FCSTD DOCUMENT  (FreeCAD 0.19R24276 (Git))
Label: Master_sketch_v2
License: All rights reserved
LicenseURL: http://en.wikipedia.org/wiki/All_rights_reserved
objects: Sketcher::SketchObject×6, PartDesign::Body×1
note: 7 computed .brp shape members not serialized (recipe doc carries the construction recipe); baked Part::Feature solids carry a one-line shape summary decoded from their .brp

FEATURE [Sketcher::SketchObject] Sketch  label="Sketch_korzina"
  FullyConstrained = false
  MapMode = 5
  Support = -> [XY_Plane]
  sketch-geometry (21):
    g0: Circle CenterX=0 CenterY=-54 CenterZ=0 NormalX=0 NormalY=0 NormalZ=1 AngleXU=0 Radius=4
    g1: LineSegment StartX=-45 StartY=0 StartZ=0 EndX=-62.2822 EndY=-37.1796 EndZ=0
    g2: LineSegment StartX=45 StartY=0 StartZ=0 EndX=62.2822 EndY=-37.1796 EndZ=0
    g3: LineSegment StartX=-45 StartY=0 StartZ=0 EndX=45 EndY=0 EndZ=0
    g4: LineSegment StartX=0 StartY=0 StartZ=0 EndX=0 EndY=-54 EndZ=0
    g5: Circle CenterX=0 CenterY=0 CenterZ=0 NormalX=0 NormalY=0 NormalZ=1 AngleXU=0 Radius=90
    g6: LineSegment StartX=-45 StartY=0 StartZ=0 EndX=-31.8819 EndY=-39.2255 EndZ=0
    g7: Circle CenterX=0 CenterY=54 CenterZ=0 NormalX=0 NormalY=0 NormalZ=1 AngleXU=0 Radius=4
    g8: LineSegment StartX=0 StartY=0 StartZ=0 EndX=0 EndY=54 EndZ=0
    g9: LineSegment StartX=45 StartY=0 StartZ=0 EndX=56.689 EndY=42.3716 EndZ=0
    g10: LineSegment StartX=-31.8413 StartY=-51.3294 StartZ=0 EndX=-28.0476 EndY=-43.1681 EndZ=0
    g11: LineSegment StartX=-31.8413 StartY=-51.3294 StartZ=0 EndX=-35.6349 EndY=-59.4908 EndZ=0
    g12: Circle CenterX=-45 CenterY=0 CenterZ=0 NormalX=0 NormalY=0 NormalZ=1 AngleXU=0 Radius=41
    g13: Circle CenterX=45 CenterY=0 CenterZ=0 NormalX=0 NormalY=0 NormalZ=1 AngleXU=0 Radius=41
    g14: Circle CenterX=0 CenterY=-54 CenterZ=0 NormalX=0 NormalY=0 NormalZ=1 AngleXU=0 Radius=11
    g15: LineSegment StartX=0 StartY=-54 StartZ=0 EndX=-4.63669 EndY=-63.975 EndZ=0
    g16: LineSegment StartX=-31.8413 StartY=-51.3294 StartZ=0 EndX=-35.6349 EndY=-59.4908 EndZ=0
    g17: LineSegment StartX=62.2822 StartY=-37.1796 StartZ=0 EndX=4.63669 EndY=-63.975 EndZ=0
    g18: LineSegment StartX=4.63669 StartY=-63.975 StartZ=0 EndX=0 EndY=-54 EndZ=0
    g19: LineSegment StartX=-62.2822 StartY=-37.1796 StartZ=0 EndX=-4.63669 EndY=-63.975 EndZ=0
    g20: LineSegment StartX=-31.8413 StartY=-51.3294 StartZ=0 EndX=-62.2822 EndY=-37.1796 EndZ=0
  constraints (45):
    c: Diameter(g0) = 8
    c: Distance(g3) = 90
    c: Coincident(g4,g-1)
    c: Coincident(g4,g0)
    c: Perpendicular(g3,g4)
    c: Distance(g4) = 54
    c: Coincident(g5,g-1)
    c: Diameter(g5) = 180
    c: Coincident(g8,g-1)
    c: Coincident(g8,g7)
    c: Equal(g8,g4)
    c: Parallel(g8,g4)
    c: Coincident(g11,g10)
    c: Symmetric(g11,g10,g10)
    c: Distance(g11,g10) = 18
    c: Coincident(g12,g1)
    c: Coincident(g13,g2)
    c: Equal(g12,g13)
    c: Coincident(g1,g3)
    c: Coincident(g6,g1)
    c: Coincident(g3,g2)
    c: Coincident(g3,g9)
    c: Symmetric(g1,g2,g-1)
    c: Horizontal(g3)
    c: PointOnObject(g1,g12)
    c: Diameter(g12) = 82
    c: Coincident(g14,g0)
    c: Diameter(g14) = 22
    c: PointOnObject(g15,g14)
    c: Coincident(g15,g0)
    c: Coincident(g10,g16)
    c: Distance(g15,g10) = 30
    c: PointOnObject(g2,g13)
    c: Coincident(g17,g2)
    c: PointOnObject(g17,g14)
    c: Coincident(g18,g0)
    c: Perpendicular(g17,g18)
    c: Perpendicular(g17,g2)
    c: Coincident(g19,g1)
    c: Perpendicular(g15,g19)
    c: Perpendicular(g19,g1)
    c: Perpendicular(g10,g19)
    c: Coincident(g20,g10)
    c: Coincident(g20,g1)
    c: Tangent(g20,g12)
FEATURE [PartDesign::Body] Body
  Group = -> [Sketch]
  Origin = -> Origin
FEATURE [Sketcher::SketchObject] Sketch001  label="Sketch001_left"
  FullyConstrained = false
  MapMode = 5
  sketch-geometry (18):
    g0: LineSegment StartX=-45 StartY=0 StartZ=0 EndX=45 EndY=0 EndZ=0
    g1: LineSegment StartX=0 StartY=0 StartZ=0 EndX=0 EndY=-54 EndZ=0
    g2: Circle CenterX=0 CenterY=54 CenterZ=0 NormalX=0 NormalY=0 NormalZ=1 AngleXU=0 Radius=4
    g3: LineSegment StartX=0 StartY=0 StartZ=0 EndX=0 EndY=54 EndZ=0
    g4: Circle CenterX=0 CenterY=220 CenterZ=0 NormalX=0 NormalY=0 NormalZ=1 AngleXU=0 Radius=20
    g5: LineSegment StartX=1.97542 StartY=-120.078 StartZ=0 EndX=-81.7197 EndY=-81.8796 EndZ=0
    g6: LineSegment StartX=-81.7197 StartY=-81.8796 StartZ=0 EndX=-106.606 EndY=-84.2618 EndZ=0
    g7: LineSegment StartX=-106.606 StartY=-84.2618 StartZ=0 EndX=-106.892 EndY=-81.2754 EndZ=0
    g8: LineSegment StartX=-106.892 StartY=-81.2754 StartZ=0 EndX=-82.0055 EndY=-78.8932 EndZ=0
    g9: LineSegment StartX=-82.0055 StartY=-78.8932 StartZ=0 EndX=-81.7197 EndY=-81.8796 EndZ=0
    g10: LineSegment StartX=-18.9589 StartY=-118.419 StartZ=0 EndX=22.9098 EndY=-121.738 EndZ=0
    g11: LineSegment StartX=22.9098 StartY=-121.738 StartZ=0 EndX=22.5147 EndY=-126.722 EndZ=0
    g12: LineSegment StartX=-19.354 StartY=-123.403 StartZ=0 EndX=-18.9589 EndY=-118.419 EndZ=0
    g13: LineSegment StartX=-18.9589 StartY=-118.419 StartZ=0 EndX=-81.7197 EndY=-81.8796 EndZ=0
    g14: LineSegment StartX=-19.354 StartY=-123.403 StartZ=0 EndX=-106.606 EndY=-84.2618 EndZ=0
    g15: LineSegment StartX=-19.354 StartY=-123.403 StartZ=0 EndX=22.5147 EndY=-126.722 EndZ=0
    g16: Circle CenterX=0 CenterY=-145 CenterZ=0 NormalX=0 NormalY=0 NormalZ=1 AngleXU=0 Radius=4
    g17: LineSegment StartX=0 StartY=-145 StartZ=0 EndX=1.97542 EndY=-120.078 EndZ=0
  constraints (47):
    c: Distance(g0) = 90
    c: Coincident(g1,g-1)
    c: Perpendicular(g0,g1)
    c: Distance(g1) = 54
    c: Coincident(g3,g-1)
    c: Coincident(g3,g2)
    c: Equal(g3,g1)
    c: Parallel(g3,g1)
    c: PointOnObject(g4,g-2)
    c: Radius(g4) = 20
    c: DistanceY(g-1,g4) = 220
    c: Distance(g5) = 92
    c: Coincident(g6,g5)
    c: Coincident(g8,g7)
    c: Coincident(g9,g8)
    c: Coincident(g9,g5)
    c: Parallel(g7,g9)
    c: Perpendicular(g7,g6)
    c: Distance(g6) = 25
    c: Symmetric(g0,g0,g-1)
    c: Horizontal(g0)
    c: Parallel(g6,g8)
    c: Angle(g6,g5) = 2.61799
    c: Coincident(g10,g11)
    c: Coincident(g12,g10)
    c: Symmetric(g10,g10,g5)
    c: Coincident(g13,g10)
    c: Coincident(g13,g5)
    c: Coincident(g14,g6)
    c: Coincident(g7,g6)
    c: Distance(g7) = 3
    c: Perpendicular(g11,g10)
    c: Angle(g5,g10) = 0.349066
    c: Equal(g12,g11)
    c: Coincident(g15,g14)
    c: Coincident(g15,g11)
    c: Coincident(g14,g12)
    c: Perpendicular(g15,g12)
    c: Distance(g14,g11) = 42
    c: Distance(g10,g11) = 5
    c: PointOnObject(g16,g-2)
    c: Diameter(g16) = 8
    c: Coincident(g17,g16)
    c: Coincident(g17,g5)
    c: Perpendicular(g15,g17)
    c: Distance(g16,g17) = 25
    c: DistanceY(g16,g-1) = 145
FEATURE [Sketcher::SketchObject] Sketch020  label="Sketch020_right"
  FullyConstrained = false
  MapMode = 5
  sketch-geometry (46):
    g0: Circle CenterX=0 CenterY=-54 CenterZ=0 NormalX=0 NormalY=0 NormalZ=1 AngleXU=0 Radius=4
    g1: LineSegment StartX=-57.9645 StartY=-38.8963 StartZ=0 EndX=-1.26483 EndY=-57.7948 EndZ=0
    g2: LineSegment StartX=-45 StartY=0 StartZ=0 EndX=-57.9645 EndY=-38.8963 EndZ=0
    g3: LineSegment StartX=0 StartY=-54 StartZ=0 EndX=-1.26483 EndY=-57.7948 EndZ=0
    g4: LineSegment StartX=1.39757 StartY=-57.7479 StartZ=0 EndX=58.5823 EndY=-36.4241 EndZ=0
    g5: LineSegment StartX=45 StartY=0 StartZ=0 EndX=58.5823 EndY=-36.4241 EndZ=0
    g6: LineSegment StartX=0 StartY=-54 StartZ=0 EndX=1.39757 EndY=-57.7479 EndZ=0
    g7: LineSegment StartX=-45 StartY=0 StartZ=0 EndX=45 EndY=0 EndZ=0
    g8: LineSegment StartX=0 StartY=0 StartZ=0 EndX=0 EndY=-54 EndZ=0
    g9: Circle CenterX=0 CenterY=0 CenterZ=0 NormalX=0 NormalY=0 NormalZ=1 AngleXU=0 Radius=90
    g10: LineSegment StartX=-45 StartY=0 StartZ=0 EndX=-31.8819 EndY=-39.2255 EndZ=0
    g11: Circle CenterX=0 CenterY=54 CenterZ=0 NormalX=0 NormalY=0 NormalZ=1 AngleXU=0 Radius=4
    g12: LineSegment StartX=0 StartY=0 StartZ=0 EndX=0 EndY=54 EndZ=0
    g13: Circle CenterX=0 CenterY=220 CenterZ=0 NormalX=0 NormalY=0 NormalZ=1 AngleXU=0 Radius=20
    g14: LineSegment StartX=45 StartY=0 StartZ=0 EndX=56.689 EndY=42.3716 EndZ=0
    g15: LineSegment StartX=-29.7255 StartY=-48.3086 StartZ=0 EndX=-26.8797 EndY=-39.7704 EndZ=0
    g16: LineSegment StartX=-29.7255 StartY=-48.3086 StartZ=0 EndX=-32.5714 EndY=-56.8468 EndZ=0
    g17: Circle CenterX=-45 CenterY=0 CenterZ=0 NormalX=0 NormalY=0 NormalZ=1 AngleXU=0 Radius=41
    g18: Circle CenterX=45 CenterY=0 CenterZ=0 NormalX=0 NormalY=0 NormalZ=1 AngleXU=0 Radius=41
    g19: LineSegment StartX=0 StartY=0 StartZ=0 EndX=0 EndY=-135 EndZ=0
    g20: LineSegment StartX=0 StartY=-135 StartZ=0 EndX=-86.4517 EndY=-103.534 EndZ=0
    g21: LineSegment StartX=0 StartY=-135 StartZ=0 EndX=86.4517 EndY=-103.534 EndZ=0
    g22: LineSegment StartX=-86.4517 StartY=-103.534 StartZ=0 EndX=-111.072 EndY=-107.875 EndZ=0
    g23: LineSegment StartX=-111.072 StartY=-107.875 StartZ=0 EndX=-111.593 EndY=-104.921 EndZ=0
    g24: LineSegment StartX=-111.593 StartY=-104.921 StartZ=0 EndX=-86.9727 EndY=-100.58 EndZ=0
    g25: LineSegment StartX=-86.9727 StartY=-100.58 StartZ=0 EndX=-86.4517 EndY=-103.534 EndZ=0
    g26: LineSegment StartX=-21 StartY=-135 StartZ=0 EndX=21 EndY=-135 EndZ=0
    g27: LineSegment StartX=21 StartY=-135 StartZ=0 EndX=21 EndY=-140 EndZ=0
    g28: LineSegment StartX=21 StartY=-140 StartZ=0 EndX=-21 EndY=-140 EndZ=0
    g29: LineSegment StartX=-21 StartY=-140 StartZ=0 EndX=-21 EndY=-135 EndZ=0
    g30: LineSegment StartX=0 StartY=-135 StartZ=0 EndX=-72.9805 EndY=-135 EndZ=0
    g31: LineSegment StartX=-21 StartY=-135 StartZ=0 EndX=-86.4517 EndY=-103.534 EndZ=0
    g32: LineSegment StartX=-21 StartY=-140 StartZ=0 EndX=-111.072 EndY=-107.875 EndZ=0
    g33: LineSegment StartX=-110.377 StartY=-111.815 StartZ=0 EndX=-61.9528 EndY=-103.276 EndZ=0
    g34: LineSegment StartX=-111.072 StartY=-107.875 StartZ=0 EndX=-110.377 EndY=-111.815 EndZ=0
    g35: LineSegment StartX=-86.9727 StartY=-100.58 StartZ=0 EndX=118.679 EndY=-100.58 EndZ=0
    g36: LineSegment StartX=86.4517 StartY=-103.534 StartZ=0 EndX=111.072 EndY=-107.875 EndZ=0
    g37: LineSegment StartX=111.072 StartY=-107.875 StartZ=0 EndX=111.593 EndY=-104.921 EndZ=0
    g38: LineSegment StartX=111.593 StartY=-104.921 StartZ=0 EndX=86.9727 EndY=-100.58 EndZ=0
    g39: LineSegment StartX=86.9727 StartY=-100.58 StartZ=0 EndX=86.4517 EndY=-103.534 EndZ=0
    g40: LineSegment StartX=21 StartY=-135 StartZ=0 EndX=-21 EndY=-135 EndZ=0
    g41: LineSegment StartX=-21 StartY=-135 StartZ=0 EndX=-21 EndY=-130 EndZ=0
    g42: LineSegment StartX=-21 StartY=-130 StartZ=0 EndX=21 EndY=-130 EndZ=0
    g43: LineSegment StartX=21 StartY=-130 StartZ=0 EndX=21 EndY=-135 EndZ=0
    g44: LineSegment StartX=21 StartY=-135 StartZ=0 EndX=111.072 EndY=-107.875 EndZ=0
    g45: LineSegment StartX=21 StartY=-130 StartZ=0 EndX=86.4517 EndY=-103.534 EndZ=0
  constraints (115):
    c: Diameter(g0) = 8
    c: PointOnObject(g1,g0)
    c: Perpendicular(g1,g2)
    c: Coincident(g3,g0)
    c: Coincident(g3,g1)
    c: Perpendicular(g3,g1)
    c: PointOnObject(g4,g0)
    c: Coincident(g5,g4)
    c: Perpendicular(g5,g4)
    c: Coincident(g6,g0)
    c: Coincident(g6,g4)
    c: Perpendicular(g4,g6)
    c: Distance(g7) = 90
    c: Coincident(g8,g-1)
    c: Coincident(g8,g0)
    c: Perpendicular(g7,g8)
    c: Distance(g8) = 54
    c: Coincident(g9,g-1)
    c: Diameter(g9) = 180
    c: Equal(g0,g11)
    c: Coincident(g12,g-1)
    c: Coincident(g12,g11)
    c: Equal(g12,g8)
    c: Parallel(g12,g8)
    c: PointOnObject(g13,g-2)
    c: Radius(g13) = 20
    c: DistanceY(g-1,g13) = 220
    c: PointOnObject(g15,g1)
    c: Coincident(g16,g15)
    c: Symmetric(g16,g15,g15)
    c: Distance(g16,g15) = 18
    c: Perpendicular(g15,g1)
    c: Distance(g15,g1) = 30
    c: Coincident(g17,g2)
    c: Coincident(g18,g5)
    c: Equal(g17,g18)
    c: Coincident(g19,g-1)
    c: Vertical(g19)
    c: DistanceY(g19,g19) = 135
    c: Coincident(g20,g21)
    c: Coincident(g20,g19)
    c: Distance(g20) = 92
    c: Equal(g20,g21)
    c: Coincident(g22,g20)
    c: Coincident(g24,g23)
    c: Coincident(g25,g24)
    c: Coincident(g25,g20)
    c: Parallel(g23,g25)
    c: Perpendicular(g23,g22)
    c: Distance(g22) = 25
    c: Coincident(g2,g7)
    c: Coincident(g10,g2)
    c: Coincident(g7,g5)
    c: Coincident(g7,g14)
    c: Symmetric(g2,g5,g-1)
    c: Horizontal(g7)
    c: PointOnObject(g2,g17)
    c: Coincident(g1,g2)
    c: Diameter(g17) = 82
    c: Parallel(g22,g24)
    c: Angle(g22,g20) = 2.61799
    c: Coincident(g26,g27)
    c: Coincident(g27,g28)
    c: Coincident(g28,g29)
    c: Coincident(g29,g26)
    c: Horizontal(g26)
    c: Horizontal(g28)
    c: Vertical(g27)
    c: Vertical(g29)
    c: Coincident(g30,g20)
    c: Horizontal(g30)
    c: Angle(g20,g30) = 0.349066
    c: DistanceX(g28,g28) = 42
    c: Symmetric(g26,g26,g20)
    c: DistanceY(g27,g27) = 5
    c: Coincident(g31,g26)
    c: Coincident(g31,g20)
    c: Coincident(g32,g28)
    c: Coincident(g32,g22)
    c: Coincident(g23,g22)
    c: Distance(g23) = 3
    c: Parallel(g22,g33)
    c: Coincident(g34,g23)
    c: Perpendicular(g34,g33)
    c: Coincident(g33,g34)
    c: Distance(g34) = 4
    c: Coincident(g35,g24)
    c: Horizontal(g35)
    c: Coincident(g38,g37)
    c: Coincident(g39,g38)
    c: Parallel(g37,g39)
    c: Perpendicular(g37,g36)
    c: Distance(g36) = 25
    c: Parallel(g36,g38)
    c: Coincident(g37,g36)
    c: Distance(g37) = 3
    c: Coincident(g21,g39)
    c: Angle(g21,g30) = 2.79253
    c: Coincident(g40,g41)
    c: Coincident(g41,g42)
    c: Coincident(g42,g43)
    c: Coincident(g43,g40)
    c: Horizontal(g40)
    c: Horizontal(g42)
    c: Vertical(g41)
    c: Vertical(g43)
    c: Coincident(g40,g26)
    c: DistanceY(g43,g43) = 5
    c: Vertical(g41,g26)
    c: Coincident(g44,g26)
    c: Coincident(g44,g37)
    c: Coincident(g45,g42)
    c: Coincident(g45,g39)
    c: Coincident(g36,g39)
    c: Angle(g21,g36) = 2.61799
FEATURE [Sketcher::SketchObject] Sketch021  label="Sketch001_left_right_lips"
  FullyConstrained = false
  MapMode = 5
  sketch-geometry (31):
    g0: LineSegment StartX=-1.5074 StartY=-120.045 StartZ=0 EndX=-89.6991 EndY=-93.8496 EndZ=0
    g1: LineSegment StartX=-89.6991 StartY=-93.8496 StartZ=0 EndX=-114.013 EndY=-99.6674 EndZ=0
    g2: LineSegment StartX=-114.013 StartY=-99.6674 StartZ=0 EndX=-114.711 EndY=-96.7497 EndZ=0
    g3: LineSegment StartX=-114.711 StartY=-96.7497 StartZ=0 EndX=-90.3972 EndY=-90.9319 EndZ=0
    g4: LineSegment StartX=-90.3972 StartY=-90.9319 StartZ=0 EndX=-89.6991 EndY=-93.8496 EndZ=0
    g5: LineSegment StartX=-22.4692 StartY=-121.312 StartZ=0 EndX=19.4544 EndY=-118.779 EndZ=0
    g6: LineSegment StartX=19.4544 StartY=-118.779 StartZ=0 EndX=19.7559 EndY=-123.77 EndZ=0
    g7: LineSegment StartX=-22.1677 StartY=-126.303 StartZ=0 EndX=-22.4692 EndY=-121.312 EndZ=0
    g8: LineSegment StartX=-22.4692 StartY=-121.312 StartZ=0 EndX=-89.6991 EndY=-93.8496 EndZ=0
    g9: LineSegment StartX=-22.1677 StartY=-126.303 StartZ=0 EndX=-114.013 EndY=-99.6674 EndZ=0
    g10: LineSegment StartX=-22.1677 StartY=-126.303 StartZ=0 EndX=19.7559 EndY=-123.77 EndZ=0
    g11: Circle CenterX=0 CenterY=-145 CenterZ=0 NormalX=0 NormalY=0 NormalZ=1 AngleXU=0 Radius=4
    g12: LineSegment StartX=0 StartY=-145 StartZ=0 EndX=-1.5074 EndY=-120.045 EndZ=0
    g13: LineSegment StartX=-22.4692 StartY=-121.312 StartZ=0 EndX=-22.7707 EndY=-116.321 EndZ=0
    g14: LineSegment StartX=19.1529 StartY=-113.788 StartZ=0 EndX=19.4544 EndY=-118.779 EndZ=0
    g15: LineSegment StartX=-22.7707 StartY=-116.321 StartZ=0 EndX=19.1529 EndY=-113.788 EndZ=0
    g16: LineSegment StartX=-1.5074 StartY=-120.045 StartZ=0 EndX=82.8898 EndY=-83.4242 EndZ=0
    g17: LineSegment StartX=82.8898 StartY=-83.4242 StartZ=0 EndX=107.727 EndY=-86.273 EndZ=0
    g18: LineSegment StartX=82.8898 StartY=-83.4242 StartZ=0 EndX=83.2316 EndY=-80.4437 EndZ=0
    g19: LineSegment StartX=107.727 StartY=-86.273 StartZ=0 EndX=108.069 EndY=-83.2925 EndZ=0
    g20: LineSegment StartX=108.069 StartY=-83.2925 StartZ=0 EndX=83.2316 EndY=-80.4437 EndZ=0
    g21: LineSegment StartX=19.4544 StartY=-118.779 StartZ=0 EndX=107.727 EndY=-86.273 EndZ=0
    g22: LineSegment StartX=19.1529 StartY=-113.788 StartZ=0 EndX=82.8898 EndY=-83.4242 EndZ=0
    g23: LineSegment StartX=-114.711 StartY=-96.7497 StartZ=0 EndX=-120.296 EndY=-73.4087 EndZ=0
    g24: LineSegment StartX=-120.296 StartY=-73.4087 StartZ=0 EndX=-95.9823 EndY=-67.5908 EndZ=0
    g25: LineSegment StartX=-95.9823 StartY=-67.5908 StartZ=0 EndX=-90.3972 EndY=-90.9319 EndZ=0
    g26: LineSegment StartX=-117.038 StartY=-87.0243 StartZ=0 EndX=-92.7244 EndY=-81.2065 EndZ=0
    g27: LineSegment StartX=83.2316 StartY=-80.4437 StartZ=0 EndX=85.9665 EndY=-56.6001 EndZ=0
    g28: LineSegment StartX=85.9665 StartY=-56.6001 StartZ=0 EndX=110.804 EndY=-59.4489 EndZ=0
    g29: LineSegment StartX=110.804 StartY=-59.4489 StartZ=0 EndX=108.069 EndY=-83.2925 EndZ=0
    g30: LineSegment StartX=84.3711 StartY=-70.5089 StartZ=0 EndX=109.208 EndY=-73.3577 EndZ=0
  constraints (84):
    c: Distance(g0) = 92
    c: Coincident(g1,g0)
    c: Coincident(g3,g2)
    c: Coincident(g4,g3)
    c: Coincident(g4,g0)
    c: Parallel(g2,g4)
    c: Perpendicular(g2,g1)
    c: Distance(g1) = 25
    c: Parallel(g1,g3)
    c: Angle(g1,g0) = 2.61799
    c: Coincident(g5,g6)
    c: Coincident(g7,g5)
    c: Symmetric(g5,g5,g0)
    c: Coincident(g8,g5)
    c: Coincident(g8,g0)
    c: Coincident(g9,g1)
    c: Coincident(g2,g1)
    c: Distance(g2) = 3
    c: Perpendicular(g6,g5)
    c: Angle(g0,g5) = 0.349066
    c: Equal(g7,g6)
    c: Coincident(g10,g9)
    c: Coincident(g10,g6)
    c: Coincident(g9,g7)
    c: Perpendicular(g10,g7)
    c: Distance(g9,g6) = 42
    c: Distance(g5,g6) = 5
    c: PointOnObject(g11,g-2)
    c: Diameter(g11) = 8
    c: Coincident(g12,g11)
    c: Coincident(g12,g0)
    c: Perpendicular(g10,g12)
    c: Distance(g11,g12) = 25
    c: DistanceY(g11,g-1) = 145
    c: Coincident(g13,g5)
    c: Perpendicular(g13,g5)
    c: Distance(g13) = 5
    c: Coincident(g14,g5)
    c: Coincident(g15,g13)
    c: Parallel(g15,g5)
    c: Equal(g15,g5)
    c: Coincident(g14,g15)
    c: Coincident(g16,g12)
    c: Angle(g5,g16) = 0.349066
    c: Equal(g16,g0)
    c: Coincident(g17,g16)
    c: Angle(g16,g17) = 2.61799
    c: Coincident(g18,g16)
    c: Coincident(g19,g17)
    c: Perpendicular(g17,g18)
    c: Perpendicular(g17,g19)
    c: Distance(g19) = 3
    c: Coincident(g20,g19)
    c: Coincident(g20,g18)
    c: Equal(g18,g19)
    c: Distance(g16,g17) = 25
    c: Coincident(g21,g5)
    c: Coincident(g21,g17)
    c: Coincident(g22,g14)
    c: Coincident(g22,g16)
    c: Coincident(g23,g2)
    c: Coincident(g24,g23)
    c: Coincident(g25,g3)
    c: Perpendicular(g23,g3)
    c: Coincident(g24,g25)
    c: Perpendicular(g25,g3)
    c: Equal(g23,g25)
    c: Distance(g23) = 24
    c: Parallel(g24,g26)
    c: PointOnObject(g26,g23)
    c: PointOnObject(g26,g25)
    c: Distance(g2,g26) = 10
    c: Coincident(g27,g18)
    c: Coincident(g28,g27)
    c: Coincident(g29,g28)
    c: Coincident(g29,g19)
    c: Perpendicular(g27,g20)
    c: Perpendicular(g20,g29)
    c: Parallel(g28,g20)
    c: Distance(g27) = 24
    c: PointOnObject(g30,g27)
    c: PointOnObject(g30,g29)
    c: Distance(g30,g18) = 10
    c: Parallel(g30,g28)
FEATURE [Sketcher::SketchObject] Sketch022  label="Sketch001_left_right_lips001"
  FullyConstrained = false
  MapMode = 5
  sketch-geometry (48):
    g0: LineSegment StartX=3.7328 StartY=-120.28 StartZ=0 EndX=-77.0516 EndY=-76.2588 EndZ=0
    g1: LineSegment StartX=-77.0516 StartY=-76.2588 StartZ=0 EndX=-102.044 EndY=-76.8753 EndZ=0
    g2: LineSegment StartX=-102.044 StartY=-76.8753 StartZ=0 EndX=-102.118 EndY=-73.8762 EndZ=0
    g3: LineSegment StartX=-102.118 StartY=-73.8762 StartZ=0 EndX=-77.1256 EndY=-73.2598 EndZ=0
    g4: LineSegment StartX=-77.1256 StartY=-73.2598 StartZ=0 EndX=-77.0516 EndY=-76.2588 EndZ=0
    g5: LineSegment StartX=-17.0318 StartY=-117.145 StartZ=0 EndX=24.4974 EndY=-123.416 EndZ=0
    g6: LineSegment StartX=24.4974 StartY=-123.416 StartZ=0 EndX=23.7508 EndY=-128.36 EndZ=0
    g7: LineSegment StartX=-17.7784 StartY=-122.089 StartZ=0 EndX=-17.0318 EndY=-117.145 EndZ=0
    g8: LineSegment StartX=-17.0318 StartY=-117.145 StartZ=0 EndX=-77.0516 EndY=-76.2588 EndZ=0
    g9: LineSegment StartX=-17.7784 StartY=-122.089 StartZ=0 EndX=-102.044 EndY=-76.8753 EndZ=0
    g10: LineSegment StartX=-17.7784 StartY=-122.089 StartZ=0 EndX=23.7508 EndY=-128.36 EndZ=0
    g11: Circle CenterX=0 CenterY=-145 CenterZ=0 NormalX=0 NormalY=0 NormalZ=1 AngleXU=0 Radius=4
    g12: LineSegment StartX=0 StartY=-145 StartZ=0 EndX=3.7328 EndY=-120.28 EndZ=0
    g13: LineSegment StartX=-17.0318 StartY=-117.145 StartZ=0 EndX=-16.2852 EndY=-112.201 EndZ=0
    g14: LineSegment StartX=25.244 StartY=-118.472 StartZ=0 EndX=24.4974 EndY=-123.416 EndZ=0
    g15: LineSegment StartX=-16.2852 StartY=-112.201 StartZ=0 EndX=25.244 EndY=-118.472 EndZ=0
    g16: LineSegment StartX=3.7328 StartY=-120.28 StartZ=0 EndX=93.9136 EndY=-102.075 EndZ=0
    g17: LineSegment StartX=93.9136 StartY=-102.075 StartZ=0 EndX=117.61 EndY=-110.044 EndZ=0
    g18: LineSegment StartX=93.9136 StartY=-102.075 StartZ=0 EndX=94.8699 EndY=-99.2319 EndZ=0
    g19: LineSegment StartX=117.61 StartY=-110.044 StartZ=0 EndX=118.566 EndY=-107.201 EndZ=0
    g20: LineSegment StartX=118.566 StartY=-107.201 StartZ=0 EndX=94.8699 EndY=-99.2319 EndZ=0
    g21: LineSegment StartX=24.4974 StartY=-123.416 StartZ=0 EndX=117.61 EndY=-110.044 EndZ=0
    g22: LineSegment StartX=25.244 StartY=-118.472 StartZ=0 EndX=93.9136 EndY=-102.075 EndZ=0
    g23: LineSegment StartX=-102.118 StartY=-73.8762 StartZ=0 EndX=-102.71 EndY=-49.8835 EndZ=0
    g24: LineSegment StartX=-102.71 StartY=-49.8835 StartZ=0 EndX=-77.7173 EndY=-49.2671 EndZ=0
    g25: LineSegment StartX=-77.7173 StartY=-49.2671 StartZ=0 EndX=-77.1256 EndY=-73.2598 EndZ=0
    g26: LineSegment StartX=-102.365 StartY=-63.8792 StartZ=0 EndX=-77.3721 EndY=-63.2628 EndZ=0
    g27: LineSegment StartX=94.8699 StartY=-99.2319 StartZ=0 EndX=102.52 EndY=-76.4837 EndZ=0
    g28: LineSegment StartX=102.52 StartY=-76.4837 StartZ=0 EndX=126.216 EndY=-84.4523 EndZ=0
    g29: LineSegment StartX=126.216 StartY=-84.4523 StartZ=0 EndX=118.566 EndY=-107.201 EndZ=0
    g30: LineSegment StartX=98.0573 StartY=-89.7535 StartZ=0 EndX=121.753 EndY=-97.7221 EndZ=0
    g31: Circle CenterX=-78.9071 CenterY=-93.0839 CenterZ=0 NormalX=0 NormalY=0 NormalZ=1 AngleXU=0 Radius=11
    g32: LineSegment StartX=3.7328 StartY=-120.28 StartZ=0 EndX=-78.9071 EndY=-93.0839 EndZ=0
    g33: LineSegment StartX=-78.9071 StartY=-93.0839 StartZ=0 EndX=64.3834 EndY=-48.7235 EndZ=0
    g34: LineSegment StartX=-79.7943 StartY=-90.2181 StartZ=0 EndX=63.4962 EndY=-45.8577 EndZ=0
    g35: LineSegment StartX=64.3834 StartY=-48.7235 StartZ=0 EndX=63.4962 EndY=-45.8577 EndZ=0
    g36: LineSegment StartX=-78.9071 StartY=-93.0839 StartZ=0 EndX=-79.7943 EndY=-90.2181 EndZ=0
    g37: Circle CenterX=0 CenterY=-54 CenterZ=0 NormalX=0 NormalY=0 NormalZ=1 AngleXU=0 Radius=11
    g38: LineSegment StartX=0 StartY=-54 StartZ=0 EndX=3.25309 EndY=-64.508 EndZ=0
    g39: LineSegment StartX=3.25309 StartY=-64.508 StartZ=0 EndX=63.4962 EndY=-45.8577 EndZ=0
    g40: Circle CenterX=-78.9071 CenterY=-93.0839 CenterZ=0 NormalX=0 NormalY=0 NormalZ=1 AngleXU=0 Radius=14
    g41: Circle CenterX=-78.9071 CenterY=-93.0839 CenterZ=0 NormalX=0 NormalY=0 NormalZ=1 AngleXU=0 Radius=2.5
    g42: LineSegment StartX=-41.5835 StartY=-78.3886 StartZ=0 EndX=-39.8091 EndY=-84.1203 EndZ=0
    g43: LineSegment StartX=-39.8091 StartY=-84.1203 StartZ=0 EndX=65.2706 EndY=-51.5893 EndZ=0
    g44: LineSegment StartX=64.3834 StartY=-48.7235 StartZ=0 EndX=65.2706 EndY=-51.5893 EndZ=0
    g45: LineSegment StartX=-78.9071 StartY=-93.0839 StartZ=0 EndX=-92.4492 EndY=-114.098 EndZ=0
    g46: LineSegment StartX=-17.7784 StartY=-122.089 StartZ=0 EndX=-55.7737 EndY=-109.585 EndZ=0
    g47: LineSegment StartX=-55.7737 StartY=-109.585 StartZ=0 EndX=-60.4628 EndY=-123.833 EndZ=0
  constraints (130):
    c: Distance(g0) = 92
    c: Coincident(g1,g0)
    c: Coincident(g3,g2)
    c: Coincident(g4,g3)
    c: Coincident(g4,g0)
    c: Parallel(g2,g4)
    c: Perpendicular(g2,g1)
    c: Distance(g1) = 25
    c: Parallel(g1,g3)
    c: Angle(g1,g0) = 2.61799
    c: Coincident(g5,g6)
    c: Coincident(g7,g5)
    c: Symmetric(g5,g5,g0)
    c: Coincident(g8,g5)
    c: Coincident(g8,g0)
    c: Coincident(g9,g1)
    c: Coincident(g2,g1)
    c: Distance(g2) = 3
    c: Perpendicular(g6,g5)
    c: Angle(g0,g5) = 0.349066
    c: Equal(g7,g6)
    c: Coincident(g10,g9)
    c: Coincident(g10,g6)
    c: Coincident(g9,g7)
    c: Perpendicular(g10,g7)
    c: Distance(g9,g6) = 42
    c: Distance(g5,g6) = 5
    c: PointOnObject(g11,g-2)
    c: Diameter(g11) = 8
    c: Coincident(g12,g11)
    c: Coincident(g12,g0)
    c: Perpendicular(g10,g12)
    c: Distance(g11,g12) = 25
    c: DistanceY(g11,g-1) = 145
    c: Coincident(g13,g5)
    c: Perpendicular(g13,g5)
    c: Distance(g13) = 5
    c: Coincident(g14,g5)
    c: Coincident(g15,g13)
    c: Parallel(g15,g5)
    c: Equal(g15,g5)
    c: Coincident(g14,g15)
    c: Coincident(g16,g12)
    c: Angle(g5,g16) = 0.349066
    c: Equal(g16,g0)
    c: Coincident(g17,g16)
    c: Angle(g16,g17) = 2.61799
    c: Coincident(g18,g16)
    c: Coincident(g19,g17)
    c: Perpendicular(g17,g18)
    c: Perpendicular(g17,g19)
    c: Distance(g19) = 3
    c: Coincident(g20,g19)
    c: Coincident(g20,g18)
    c: Equal(g18,g19)
    c: Distance(g16,g17) = 25
    c: Coincident(g21,g5)
    c: Coincident(g21,g17)
    c: Coincident(g22,g14)
    c: Coincident(g22,g16)
    c: Coincident(g23,g2)
    c: Coincident(g24,g23)
    c: Coincident(g25,g3)
    c: Perpendicular(g23,g3)
    c: Coincident(g24,g25)
    c: Perpendicular(g25,g3)
    c: Equal(g23,g25)
    c: Distance(g23) = 24
    c: Parallel(g24,g26)
    c: PointOnObject(g26,g23)
    c: PointOnObject(g26,g25)
    c: Distance(g2,g26) = 10
    c: Coincident(g27,g18)
    c: Coincident(g28,g27)
    c: Coincident(g29,g28)
    c: Coincident(g29,g19)
    c: Perpendicular(g27,g20)
    c: Perpendicular(g20,g29)
    c: Parallel(g28,g20)
    c: Distance(g27) = 24
    c: PointOnObject(g30,g27)
    c: PointOnObject(g30,g29)
    c: Distance(g30,g18) = 10
    c: Parallel(g30,g28)
    c: Coincident(g32,g12)
    c: Coincident(g32,g31)
    c: Coincident(g33,g31)
    c: Distance(g32) = 87
    c: Distance(g33) = 150
    c: Angle(g9,g32) = 0.174533
    c: Coincident(g35,g33)
    c: Coincident(g35,g34)
    c: Perpendicular(g33,g35)
    c: Distance(g35) = 3
    c: Parallel(g34,g33)
    c: Coincident(g36,g31)
    c: Perpendicular(g33,g36)
    c: Coincident(g36,g34)
    c: PointOnObject(g37,g-2)
    c: DistanceY(g11,g37) = 91
    c: Coincident(g38,g37)
    c: PointOnObject(g38,g37)
    c: Coincident(g39,g38)
    c: Coincident(g39,g34)
    c: Parallel(g39,g34)
    c: Diameter(g37) = 22
    c: Perpendicular(g38,g34)
    c: Equal(g31,g37)
    c: Coincident(g40,g31)
    c: Diameter(g40) = 28
    c: Coincident(g41,g31)
    c: Diameter(g41) = 5
    c: PointOnObject(g42,g34)
    c: Perpendicular(g34,g42)
    c: Coincident(g43,g42)
    c: Parallel(g33,g43)
    c: Distance(g42) = 6
    c: Coincident(g44,g33)
    c: Perpendicular(g44,g33)
    c: Coincident(g44,g43)
    c: Distance(g43) = 110
    c: Coincident(g45,g31)
    c: Coincident(g46,g9)
    c: Coincident(g47,g46)
    c: Parallel(g32,g46)
    c: Distance(g46) = 40
    c: Perpendicular(g46,g47)
    c: Distance(g47) = 15
    c: Angle(g45,g33) = 2.44346
    c: Distance(g45) = 25
FEATURE [Sketcher::SketchObject] Sketch023  label="Sketch001_bear_holder"
  FullyConstrained = false
  MapMode = 5
  sketch-geometry (50):
    g0: LineSegment StartX=4.58936 StartY=-120.425 StartZ=0 EndX=-74.6169 EndY=-73.6234 EndZ=0
    g1: LineSegment StartX=-74.6169 StartY=-73.6234 StartZ=0 EndX=-99.6156 EndY=-73.3712 EndZ=0
    g2: LineSegment StartX=-99.6156 StartY=-73.3712 StartZ=0 EndX=-99.5853 EndY=-70.3714 EndZ=0
    g3: LineSegment StartX=-99.5853 StartY=-70.3714 StartZ=0 EndX=-74.5866 EndY=-70.6236 EndZ=0
    g4: LineSegment StartX=-74.5866 StartY=-70.6236 StartZ=0 EndX=-74.6169 EndY=-73.6234 EndZ=0
    g5: LineSegment StartX=-16.0538 StartY=-116.57 StartZ=0 EndX=25.2325 EndY=-124.28 EndZ=0
    g6: LineSegment StartX=25.2325 StartY=-124.28 StartZ=0 EndX=24.3146 EndY=-129.195 EndZ=0
    g7: LineSegment StartX=-16.9716 StartY=-121.485 StartZ=0 EndX=-16.0538 EndY=-116.57 EndZ=0
    g8: LineSegment StartX=-16.0538 StartY=-116.57 StartZ=0 EndX=-74.6169 EndY=-73.6234 EndZ=0
    g9: LineSegment StartX=-16.9716 StartY=-121.485 StartZ=0 EndX=-99.6156 EndY=-73.3712 EndZ=0
    g10: LineSegment StartX=-16.9716 StartY=-121.485 StartZ=0 EndX=24.3146 EndY=-129.195 EndZ=0
    g11: Circle CenterX=0 CenterY=-145 CenterZ=0 NormalX=0 NormalY=0 NormalZ=1 AngleXU=0 Radius=4
    g12: LineSegment StartX=0 StartY=-145 StartZ=0 EndX=4.58936 EndY=-120.425 EndZ=0
    g13: LineSegment StartX=-16.0538 StartY=-116.57 StartZ=0 EndX=-15.1359 EndY=-111.655 EndZ=0
    g14: LineSegment StartX=26.1504 StartY=-119.365 StartZ=0 EndX=25.2325 EndY=-124.28 EndZ=0
    g15: LineSegment StartX=-15.1359 StartY=-111.655 StartZ=0 EndX=26.1504 EndY=-119.365 EndZ=0
    g16: LineSegment StartX=4.58936 StartY=-120.425 StartZ=0 EndX=95.3482 EndY=-105.364 EndZ=0
    g17: LineSegment StartX=95.3482 StartY=-105.364 StartZ=0 EndX=118.753 EndY=-114.151 EndZ=0
    g18: LineSegment StartX=95.3482 StartY=-105.364 StartZ=0 EndX=96.4027 EndY=-102.555 EndZ=0
    g19: LineSegment StartX=118.753 StartY=-114.151 StartZ=0 EndX=119.808 EndY=-111.343 EndZ=0
    g20: LineSegment StartX=119.808 StartY=-111.343 StartZ=0 EndX=96.4027 EndY=-102.555 EndZ=0
    g21: LineSegment StartX=25.2325 StartY=-124.28 StartZ=0 EndX=118.753 EndY=-114.151 EndZ=0
    g22: LineSegment StartX=26.1504 StartY=-119.365 StartZ=0 EndX=95.3482 EndY=-105.364 EndZ=0
    g23: LineSegment StartX=-99.5853 StartY=-70.3714 StartZ=0 EndX=-99.3432 EndY=-46.3726 EndZ=0
    g24: LineSegment StartX=-99.3432 StartY=-46.3726 StartZ=0 EndX=-74.3445 EndY=-46.6248 EndZ=0
    g25: LineSegment StartX=-74.3445 StartY=-46.6248 StartZ=0 EndX=-74.5866 EndY=-70.6236 EndZ=0
    g26: LineSegment StartX=-99.4844 StartY=-60.3719 StartZ=0 EndX=-74.4857 EndY=-60.6241 EndZ=0
    g27: LineSegment StartX=96.4027 StartY=-102.555 StartZ=0 EndX=104.838 EndY=-80.0868 EndZ=0
    g28: LineSegment StartX=104.838 StartY=-80.0868 StartZ=0 EndX=128.243 EndY=-88.8739 EndZ=0
    g29: LineSegment StartX=128.243 StartY=-88.8739 StartZ=0 EndX=119.808 EndY=-111.343 EndZ=0
    g30: LineSegment StartX=99.9175 StartY=-93.1935 StartZ=0 EndX=123.322 EndY=-101.981 EndZ=0
    g31: LineSegment StartX=4.58936 StartY=-120.425 StartZ=0 EndX=-86.1191 EndY=-95.7679 EndZ=0
    g32: LineSegment StartX=-86.1191 StartY=-95.7679 StartZ=0 EndX=66.5069 EndY=-47.7546 EndZ=0
    g33: LineSegment StartX=-87.0194 StartY=-92.9061 StartZ=0 EndX=65.6067 EndY=-44.8928 EndZ=0
    g34: LineSegment StartX=66.5069 StartY=-47.7546 StartZ=0 EndX=65.6067 EndY=-44.8928 EndZ=0
    g35: Circle CenterX=0 CenterY=-54 CenterZ=0 NormalX=0 NormalY=0 NormalZ=1 AngleXU=0 Radius=11
    g36: LineSegment StartX=0 StartY=-54 StartZ=0 EndX=3.30092 EndY=-64.493 EndZ=0
    g37: LineSegment StartX=3.30092 StartY=-64.493 StartZ=0 EndX=65.6067 EndY=-44.8928 EndZ=0
    g38: Circle CenterX=-86.1191 CenterY=-95.7679 CenterZ=0 NormalX=0 NormalY=0 NormalZ=1 AngleXU=0 Radius=8
    g39: Circle CenterX=-86.1191 CenterY=-95.7679 CenterZ=0 NormalX=0 NormalY=0 NormalZ=1 AngleXU=0 Radius=2.5
    g40: LineSegment StartX=-39.3237 StartY=-77.902 StartZ=0 EndX=-37.5232 EndY=-83.6254 EndZ=0
    g41: LineSegment StartX=-37.5232 StartY=-83.6254 StartZ=0 EndX=67.4072 EndY=-50.6163 EndZ=0
    g42: LineSegment StartX=66.5069 StartY=-47.7546 StartZ=0 EndX=67.4072 EndY=-50.6163 EndZ=0
    g43: LineSegment StartX=-16.9716 StartY=-121.485 StartZ=0 EndX=-55.571 EndY=-110.992 EndZ=0
    g44: LineSegment StartX=-55.571 StartY=-110.992 StartZ=0 EndX=-59.5056 EndY=-125.467 EndZ=0
    g45: LineSegment StartX=26.1504 StartY=-119.365 StartZ=0 EndX=27.0682 EndY=-114.45 EndZ=0
    g46: Circle CenterX=-86.1191 CenterY=-95.7679 CenterZ=0 NormalX=0 NormalY=0 NormalZ=1 AngleXU=0 Radius=13
    g47: LineSegment StartX=-86.1191 StartY=-95.7679 StartZ=0 EndX=-87.0194 EndY=-92.9061 EndZ=0
    g48: LineSegment StartX=-15.1359 StartY=-111.655 StartZ=0 EndX=-134.505 EndY=-89.3629 EndZ=0
    g49: LineSegment StartX=27.0682 StartY=-114.45 StartZ=0 EndX=-138.797 EndY=-83.4748 EndZ=0
  constraints (134):
    c: Distance(g0) = 92
    c: Coincident(g1,g0)
    c: Coincident(g3,g2)
    c: Coincident(g4,g3)
    c: Coincident(g4,g0)
    c: Parallel(g2,g4)
    c: Perpendicular(g2,g1)
    c: Distance(g1) = 25
    c: Parallel(g1,g3)
    c: Angle(g1,g0) = 2.61799
    c: Coincident(g5,g6)
    c: Coincident(g7,g5)
    c: Symmetric(g5,g5,g0)
    c: Coincident(g8,g5)
    c: Coincident(g8,g0)
    c: Coincident(g9,g1)
    c: Coincident(g2,g1)
    c: Distance(g2) = 3
    c: Perpendicular(g6,g5)
    c: Angle(g0,g5) = 0.349066
    c: Equal(g7,g6)
    c: Coincident(g10,g9)
    c: Coincident(g10,g6)
    c: Coincident(g9,g7)
    c: Perpendicular(g10,g7)
    c: Distance(g9,g6) = 42
    c: Distance(g5,g6) = 5
    c: PointOnObject(g11,g-2)
    c: Diameter(g11) = 8
    c: Coincident(g12,g11)
    c: Coincident(g12,g0)
    c: Perpendicular(g10,g12)
    c: Distance(g11,g12) = 25
    c: DistanceY(g11,g-1) = 145
    c: Coincident(g13,g5)
    c: Perpendicular(g13,g5)
    c: Distance(g13) = 5
    c: Coincident(g14,g5)
    c: Coincident(g15,g13)
    c: Parallel(g15,g5)
    c: Equal(g15,g5)
    c: Coincident(g14,g15)
    c: Coincident(g16,g12)
    c: Angle(g5,g16) = 0.349066
    c: Equal(g16,g0)
    c: Coincident(g17,g16)
    c: Angle(g16,g17) = 2.61799
    c: Coincident(g18,g16)
    c: Coincident(g19,g17)
    c: Perpendicular(g17,g18)
    c: Perpendicular(g17,g19)
    c: Distance(g19) = 3
    c: Coincident(g20,g19)
    c: Coincident(g20,g18)
    c: Equal(g18,g19)
    c: Distance(g16,g17) = 25
    c: Coincident(g21,g5)
    c: Coincident(g21,g17)
    c: Coincident(g22,g14)
    c: Coincident(g22,g16)
    c: Coincident(g23,g2)
    c: Coincident(g24,g23)
    c: Coincident(g25,g3)
    c: Perpendicular(g23,g3)
    c: Coincident(g24,g25)
    c: Perpendicular(g25,g3)
    c: Equal(g23,g25)
    c: Distance(g23) = 24
    c: Parallel(g24,g26)
    c: PointOnObject(g26,g23)
    c: PointOnObject(g26,g25)
    c: Distance(g2,g26) = 10
    c: Coincident(g27,g18)
    c: Coincident(g28,g27)
    c: Coincident(g29,g28)
    c: Coincident(g29,g19)
    c: Perpendicular(g27,g20)
    c: Perpendicular(g20,g29)
    c: Parallel(g28,g20)
    c: Distance(g27) = 24
    c: PointOnObject(g30,g27)
    c: PointOnObject(g30,g29)
    c: Distance(g30,g18) = 10
    c: Parallel(g30,g28)
    c: Coincident(g31,g12)
    c: Distance(g31) = 94
    c: Distance(g32) = 160
    c: Angle(g9,g31) = 0.261799
    c: Coincident(g34,g32)
    c: Coincident(g34,g33)
    c: Perpendicular(g32,g34)
    c: Distance(g34) = 3
    c: Parallel(g33,g32)
    c: PointOnObject(g35,g-2)
    c: DistanceY(g11,g35) = 91
    c: Coincident(g36,g35)
    c: PointOnObject(g36,g35)
    c: Coincident(g37,g36)
    c: Coincident(g37,g33)
    c: Parallel(g37,g33)
    c: Diameter(g35) = 22
    c: Perpendicular(g36,g33)
    c: Diameter(g38) = 16
    c: Diameter(g39) = 5
    c: PointOnObject(g40,g33)
    c: Perpendicular(g33,g40)
    c: Coincident(g41,g40)
    c: Parallel(g32,g41)
    c: Distance(g40) = 6
    c: Coincident(g42,g32)
    c: Perpendicular(g42,g32)
    c: Coincident(g42,g41)
    c: Distance(g41) = 110
    c: Coincident(g43,g9)
    c: Coincident(g44,g43)
    c: Parallel(g31,g43)
    c: Distance(g43) = 40
    c: Perpendicular(g43,g44)
    c: Distance(g44) = 15
    c: Coincident(g45,g15)
    c: Coincident(g46,g31)
    c: Diameter(g46) = 26
    c: Coincident(g38,g31)
    c: Coincident(g31,g39)
    c: Coincident(g32,g31)
    c: Coincident(g47,g31)
    c: Perpendicular(g32,g47)
    c: Coincident(g47,g33)
    c: Coincident(g48,g13)
    c: Parallel(g15,g48)
    c: Parallel(g49,g48)
    c: Perpendicular(g45,g15)
    c: Coincident(g49,g45)
    c: Distance(g45) = 5
